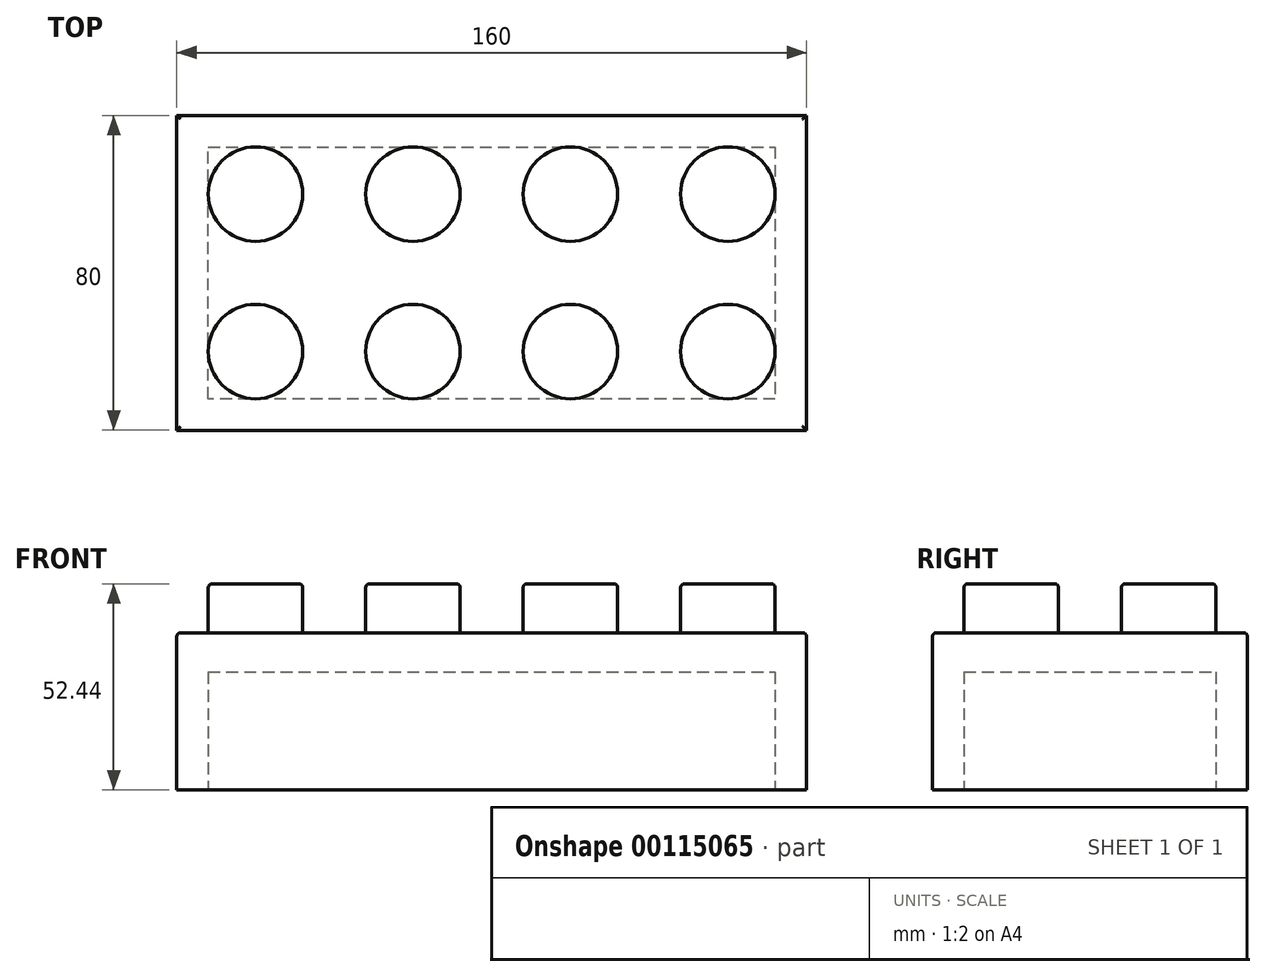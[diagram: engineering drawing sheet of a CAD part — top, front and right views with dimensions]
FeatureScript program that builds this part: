
annotation { "Feature Type Name" : "Feature", "Feature Type Description" : "" }
export const myFeature = defineFeature(function(context is Context, id is Id, definition is map)
    precondition{}
    {
        {
            var Q0;
            Q0=qCreatedBy(makeId("Top.planeOp"),FACE);
            var sketch = newSketch(context, id + "F0", { "sketchPlane" : qUnion([Q0])});
            skLineSegment(sketch, "E0", {"start": v(-64.3, 45.72) * mm, "end": v(95.7, 45.72) * mm});
            skLineSegment(sketch, "E1", {"start": v(-64.3, 45.72) * mm, "end": v(-64.3, -34.28) * mm});
            skLineSegment(sketch, "E2", {"start": v(-64.3, -34.28) * mm, "end": v(95.7, -34.28) * mm});
            skLineSegment(sketch, "E3", {"start": v(95.7, -34.28) * mm, "end": v(95.7, 45.72) * mm});
            skSolve(sketch);
        }
        {
            var Q0;
            Q0 = qSketchRegion(id + "F0", true);
            extrude(context, id + "F1", {"entities" : qUnion([Q0]), "depth" : 40 * mm});
        }
        {
            var Q0;
            Q0=makeQuery(id+"F1.opExtrude","CAP_FACE",FACE,{"disambiguationData":[OSD([sQuery(id+"F0.wireOp",EDGE,"E0"),sQuery(id+"F0.wireOp",EDGE,"E1"),sQuery(id+"F0.wireOp",EDGE,"E2"),sQuery(id+"F0.wireOp",EDGE,"E3")])],"isStart":true});
            var sketch = newSketch(context, id + "F2", { "sketchPlane" : qUnion([Q0])});
            skLineSegment(sketch, "E4.0", {"start": v(-56.32, -37.73) * mm, "end": v(87.7, -37.73) * mm});
            skLineSegment(sketch, "E4.1", {"start": v(-56.32, 26.3) * mm, "end": v(-56.32, -37.73) * mm});
            skLineSegment(sketch, "E4.2", {"start": v(87.7, 26.3) * mm, "end": v(-56.32, 26.3) * mm});
            skLineSegment(sketch, "E4.3", {"start": v(87.7, -37.73) * mm, "end": v(87.7, 26.3) * mm});
            skSolve(sketch);
        }
        {
            var Q0;
            Q0 = qSketchRegion(id + "F2", true);
            extrude(context, id + "F3", {"entities" : qUnion([Q0]), "operationType" : NewBodyOperationType.REMOVE, "oppositeDirection" : true, "depth" : 30 * mm});
        }
        {
            var Q0;
            Q0=makeQuery(id+"F1.opExtrude","CAP_FACE",FACE,{"disambiguationData":[OSD([sQuery(id+"F0.wireOp",EDGE,"E0"),sQuery(id+"F0.wireOp",EDGE,"E1"),sQuery(id+"F0.wireOp",EDGE,"E2"),sQuery(id+"F0.wireOp",EDGE,"E3")])],"isStart":false});
            var sketch = newSketch(context, id + "F4", { "sketchPlane" : qUnion([Q0])});
            skCircle(sketch, "E5", {"center": v(-44.3, 25.72) * mm, "radius": 12 * mm});
            skCircle(sketch, "E6.0.1.0", {"center": v(-44.3, -14.28) * mm, "radius": 12 * mm});
            skCircle(sketch, "E6.1.0.0", {"center": v(-4.3, 25.72) * mm, "radius": 12 * mm});
            skCircle(sketch, "E6.1.1.0", {"center": v(-4.3, -14.28) * mm, "radius": 12 * mm});
            skCircle(sketch, "E6.2.0.0", {"center": v(35.7, 25.72) * mm, "radius": 12 * mm});
            skCircle(sketch, "E6.2.1.0", {"center": v(35.7, -14.28) * mm, "radius": 12 * mm});
            skCircle(sketch, "E6.3.0.0", {"center": v(75.7, 25.72) * mm, "radius": 12 * mm});
            skCircle(sketch, "E6.3.1.0", {"center": v(75.7, -14.28) * mm, "radius": 12 * mm});
            skLineSegment(sketch, "E6.direction1", {"start": v(-44.3, 25.72) * mm, "end": v(-4.3, 25.72) * mm, "construction": true});
            skLineSegment(sketch, "E6.direction2", {"start": v(-44.3, 25.72) * mm, "end": v(-44.3, -14.28) * mm, "construction": true});
            skSolve(sketch);
        }
        {
            var Q0;
            Q0=makeQuery(id+"FpL7GTVTUkSIZti_1.opExtrude","CAP_FACE",FACE,{"disambiguationData":[OSD([sQuery(id+"F4.wireOp",EDGE,"E5")])],"isStart":false});
            var Q1;
            Q1=makeQuery(id+"FpL7GTVTUkSIZti_1.opExtrude","CAP_FACE",FACE,{"disambiguationData":[OSD([sQuery(id+"F4.wireOp",EDGE,"E6.1.0.0")])],"isStart":false});
            var Q2;
            Q2=makeQuery(id+"FpL7GTVTUkSIZti_1.opExtrude","CAP_FACE",FACE,{"disambiguationData":[OSD([sQuery(id+"F4.wireOp",EDGE,"E6.2.0.0")])],"isStart":false});
            var Q3;
            Q3=makeQuery(id+"FpL7GTVTUkSIZti_1.opExtrude","CAP_FACE",FACE,{"disambiguationData":[OSD([sQuery(id+"F4.wireOp",EDGE,"E6.3.0.0")])],"isStart":false});
            var Q4;
            Q4=makeQuery(id+"FpL7GTVTUkSIZti_1.opExtrude","CAP_FACE",FACE,{"disambiguationData":[OSD([sQuery(id+"F4.wireOp",EDGE,"E6.0.1.0")])],"isStart":false});
            var Q5;
            Q5=makeQuery(id+"FpL7GTVTUkSIZti_1.opExtrude","CAP_FACE",FACE,{"disambiguationData":[OSD([sQuery(id+"F4.wireOp",EDGE,"E6.1.1.0")])],"isStart":false});
            var Q6;
            Q6=makeQuery(id+"FpL7GTVTUkSIZti_1.opExtrude","CAP_FACE",FACE,{"disambiguationData":[OSD([sQuery(id+"F4.wireOp",EDGE,"E6.2.1.0")])],"isStart":false});
            var Q7;
            Q7=makeQuery(id+"FpL7GTVTUkSIZti_1.opExtrude","CAP_FACE",FACE,{"disambiguationData":[OSD([sQuery(id+"F4.wireOp",EDGE,"E6.3.1.0")])],"isStart":false});
            var Q8;
            Q8=makeQuery(id+"F1.opExtrude","CAP_FACE",FACE,{"disambiguationData":[OSD([sQuery(id+"F0.wireOp",EDGE,"E0"),sQuery(id+"F0.wireOp",EDGE,"E1"),sQuery(id+"F0.wireOp",EDGE,"E2"),sQuery(id+"F0.wireOp",EDGE,"E3")])],"isStart":false});
            fillet(context, id + "F5", {"entities" : qUnion([Q0, Q1, Q2, Q3, Q4, Q5, Q6, Q7, Q8]), "radius" : 1 * mm, "tangentPropagation" : true, "allowEdgeOverflow" : false});
        }
        {
            var Q0;
            Q0=makeQuery(id+"F4.imprint","IMPRINT",FACE,{"disambiguationData":[TD([[makeQuery(id+"F4.imprint","IMPRINT",EDGE,{"derivedFrom":sQuery(id+"F4.wireOp",EDGE,"E6.0.1.0")}),1.0]])]});
            var Q1;
            Q1=makeQuery(id+"F4.imprint","IMPRINT",FACE,{"disambiguationData":[TD([[makeQuery(id+"F4.imprint","IMPRINT",EDGE,{"derivedFrom":sQuery(id+"F4.wireOp",EDGE,"E6.1.1.0")}),1.0]])]});
            var Q2;
            Q2=makeQuery(id+"F4.imprint","IMPRINT",FACE,{"disambiguationData":[TD([[makeQuery(id+"F4.imprint","IMPRINT",EDGE,{"derivedFrom":sQuery(id+"F4.wireOp",EDGE,"E6.2.1.0")}),1.0]])]});
            var Q3;
            Q3=makeQuery(id+"F4.imprint","IMPRINT",FACE,{"disambiguationData":[TD([[makeQuery(id+"F4.imprint","IMPRINT",EDGE,{"derivedFrom":sQuery(id+"F4.wireOp",EDGE,"E6.3.1.0")}),1.0]])]});
            var Q4;
            Q4=makeQuery(id+"F4.imprint","IMPRINT",FACE,{"disambiguationData":[TD([[makeQuery(id+"F4.imprint","IMPRINT",EDGE,{"derivedFrom":sQuery(id+"F4.wireOp",EDGE,"E6.3.0.0")}),1.0]])]});
            var Q5;
            Q5=makeQuery(id+"F4.imprint","IMPRINT",FACE,{"disambiguationData":[TD([[makeQuery(id+"F4.imprint","IMPRINT",EDGE,{"derivedFrom":sQuery(id+"F4.wireOp",EDGE,"E6.2.0.0")}),1.0]])]});
            var Q6;
            Q6=makeQuery(id+"F4.imprint","IMPRINT",FACE,{"disambiguationData":[TD([[makeQuery(id+"F4.imprint","IMPRINT",EDGE,{"derivedFrom":sQuery(id+"F4.wireOp",EDGE,"E6.1.0.0")}),1.0]])]});
            var Q7;
            Q7=makeQuery(id+"F4.imprint","IMPRINT",FACE,{"disambiguationData":[TD([[makeQuery(id+"F4.imprint","IMPRINT",EDGE,{"derivedFrom":sQuery(id+"F4.wireOp",EDGE,"E5")}),1.0]])]});
            extrude(context, id + "F6", {"entities" : qUnion([Q0, Q1, Q2, Q3, Q4, Q5, Q6, Q7]), "operationType" : NewBodyOperationType.ADD, "depth" : 12.44 * mm});
        }
        {
            var Q0;
            Q0=makeQuery(id+"F6.opExtrude","CAP_EDGE",EDGE,{"disambiguationData":[OSD([sQuery(id+"F4.wireOp",EDGE,"E5")])],"isStart":false});
            fillet(context, id + "F7", {"entities" : qUnion([Q0]), "radius" : 1 * mm, "tangentPropagation" : true, "allowEdgeOverflow" : false});
        }
        {
            var Q0;
            Q0=makeQuery(id+"F6.opExtrude","CAP_EDGE",EDGE,{"disambiguationData":[OSD([sQuery(id+"F4.wireOp",EDGE,"E6.1.0.0")])],"isStart":false});
            fillet(context, id + "F8", {"entities" : qUnion([Q0]), "radius" : 1 * mm, "tangentPropagation" : true, "allowEdgeOverflow" : false});
        }
        {
            var Q0;
            Q0=makeQuery(id+"F6.opExtrude","CAP_EDGE",EDGE,{"disambiguationData":[OSD([sQuery(id+"F4.wireOp",EDGE,"E6.2.0.0")])],"isStart":false});
            fillet(context, id + "F9", {"entities" : qUnion([Q0]), "radius" : 1 * mm, "tangentPropagation" : true, "allowEdgeOverflow" : false});
        }
        {
            var Q0;
            Q0=makeQuery(id+"F6.opExtrude","CAP_EDGE",EDGE,{"disambiguationData":[OSD([sQuery(id+"F4.wireOp",EDGE,"E6.3.0.0")])],"isStart":false});
            fillet(context, id + "F10", {"entities" : qUnion([Q0]), "radius" : 1 * mm, "tangentPropagation" : true, "allowEdgeOverflow" : false});
        }
        {
            var Q0;
            Q0=makeQuery(id+"F6.opExtrude","CAP_EDGE",EDGE,{"disambiguationData":[OSD([sQuery(id+"F4.wireOp",EDGE,"E6.0.1.0")])],"isStart":false});
            fillet(context, id + "F11", {"entities" : qUnion([Q0]), "radius" : 1 * mm, "tangentPropagation" : true, "allowEdgeOverflow" : false});
        }
        {
            var Q0;
            Q0=makeQuery(id+"F6.opExtrude","CAP_EDGE",EDGE,{"disambiguationData":[OSD([sQuery(id+"F4.wireOp",EDGE,"E6.1.1.0")])],"isStart":false});
            fillet(context, id + "F12", {"entities" : qUnion([Q0]), "radius" : 1 * mm, "tangentPropagation" : true, "allowEdgeOverflow" : false});
        }
        {
            var Q0;
            Q0=makeQuery(id+"F6.opExtrude","CAP_EDGE",EDGE,{"disambiguationData":[OSD([sQuery(id+"F4.wireOp",EDGE,"E6.2.1.0")])],"isStart":false});
            fillet(context, id + "F13", {"entities" : qUnion([Q0]), "radius" : 1 * mm, "tangentPropagation" : true, "allowEdgeOverflow" : false});
        }
        {
            var Q0;
            Q0=makeQuery(id+"F6.opExtrude","CAP_EDGE",EDGE,{"disambiguationData":[OSD([sQuery(id+"F4.wireOp",EDGE,"E6.3.1.0")])],"isStart":false});
            fillet(context, id + "F14", {"entities" : qUnion([Q0]), "radius" : 1 * mm, "tangentPropagation" : true, "allowEdgeOverflow" : false});
        }
    });
